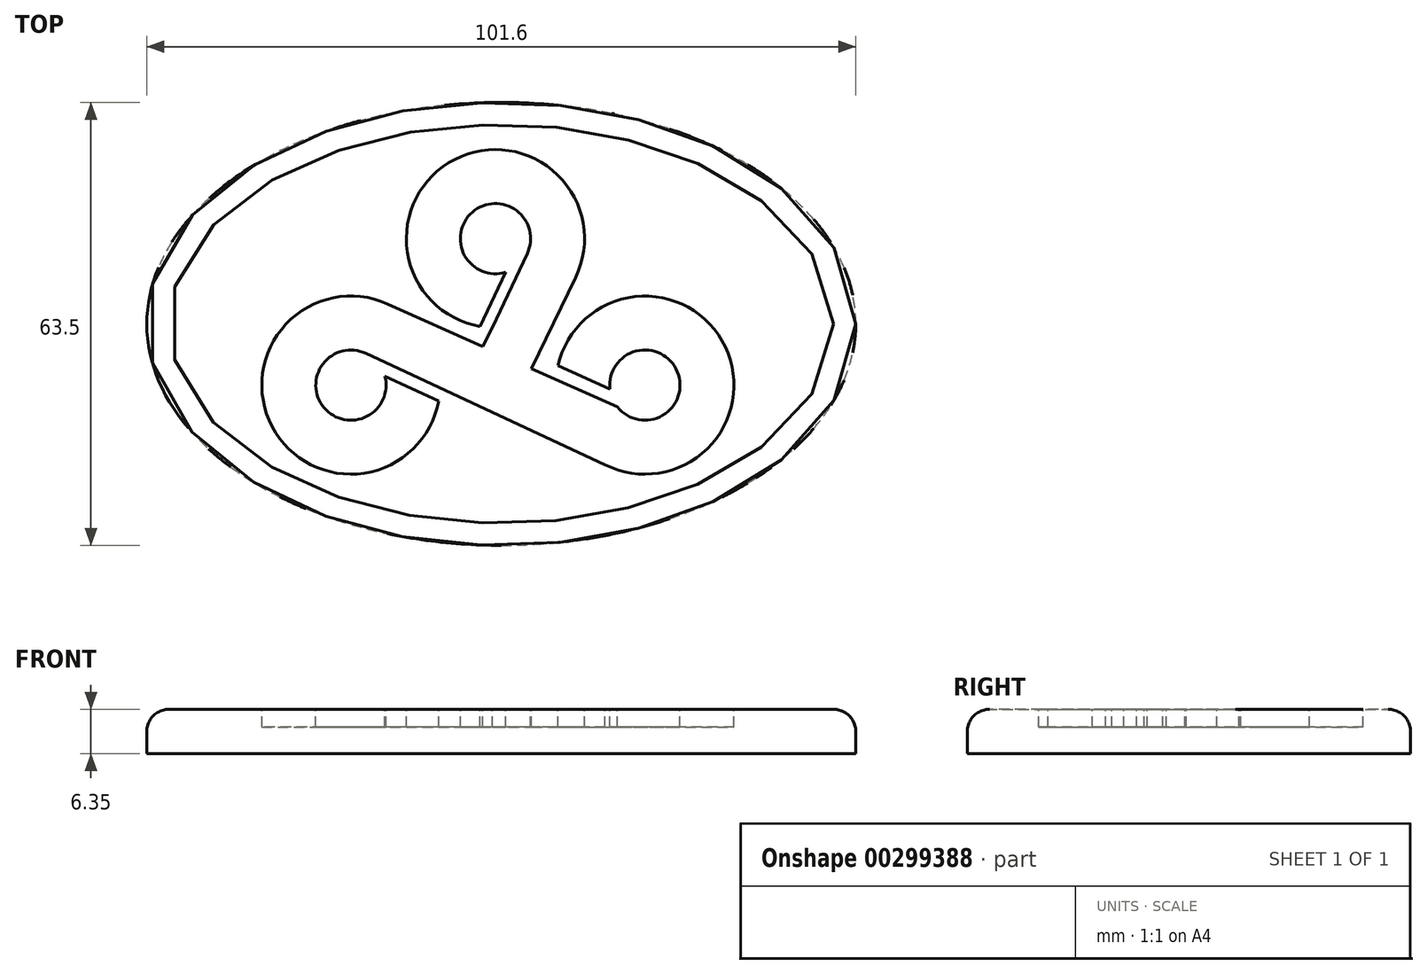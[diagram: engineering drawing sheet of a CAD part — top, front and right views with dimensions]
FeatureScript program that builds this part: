
annotation { "Feature Type Name" : "Feature", "Feature Type Description" : "" }
export const myFeature = defineFeature(function(context is Context, id is Id, definition is map)
    precondition{}
    {
        {
            var Q0;
            Q0=qCreatedBy(makeId("Top.planeOp"),FACE);
            var sketch = newSketch(context, id + "F0", { "sketchPlane" : qUnion([Q0])});
            skEllipse(sketch, "E0", {"center": v(-4.33, 14.7) * mm, "majorRadius": 50.8 * mm, "minorRadius": 31.75 * mm, "majorAxis": v(1, 0)});
            skSolve(sketch);
        }
        {
            var Q0;
            Q0=makeQuery(id+"F0.imprint","IMPRINT",FACE,{"disambiguationData":[TD([[makeQuery(id+"F0.imprint","IMPRINT",EDGE,{"derivedFrom":sQuery(id+"F0.wireOp",EDGE,"E0")}),1.0]])]});
            extrude(context, id + "F1", {"entities" : qUnion([Q0]), "depth" : 6.35 * mm});
        }
        {
            var Q0;
            Q0=makeQuery(id+"F1.opExtrude","CAP_EDGE",EDGE,{"disambiguationData":[OSD([sQuery(id+"F0.wireOp",EDGE,"E0")])],"isStart":false});
            fillet(context, id + "F2", {"entities" : qUnion([Q0]), "radius" : 3.17 * mm, "tangentPropagation" : true, "allowEdgeOverflow" : false});
        }
        {
            var Q0;
            Q0=makeQuery(id+"F1.opExtrude","CAP_FACE",FACE,{"disambiguationData":[OSD([sQuery(id+"F0.wireOp",EDGE,"E0")])],"isStart":false});
            var sketch = newSketch(context, id + "F3", { "sketchPlane" : qUnion([Q0])});
            skArc(sketch, "E1", {"start": v(-20.66, 17.57) * mm, "mid": v(-37.18, -0.02) * mm, "end": v(-13.32, 3.64) * mm});
            skArc(sketch, "E2", {"start": v(-23.75, 10.48) * mm, "mid": v(-29.73, 2.69) * mm, "end": v(-21.02, 7.22) * mm});
            skArc(sketch, "E3", {"start": v(6.32, 21.35) * mm, "mid": v(-11, 38.28) * mm, "end": v(-7.35, 14.34) * mm});
            skArc(sketch, "E4", {"start": v(-0.61, 24.78) * mm, "mid": v(-8.46, 30.72) * mm, "end": v(-3.7, 22.1) * mm});
            skArc(sketch, "E5", {"start": v(10.55, -5.5) * mm, "mid": v(27.78, 11.4) * mm, "end": v(3.8, 8.7) * mm});
            skArc(sketch, "E6", {"start": v(12.32, 2.79) * mm, "mid": v(20.9, 7.84) * mm, "end": v(11.25, 5.37) * mm});
            skLineSegment(sketch, "E7", {"start": v(-5.6, 14.16) * mm, "end": v(-7.01, 11.46) * mm});
            skLineSegment(sketch, "E8", {"start": v(-7.01, 11.46) * mm, "end": v(-20.66, 17.57) * mm});
            skLineSegment(sketch, "E9", {"start": v(-20.66, 17.57) * mm, "end": v(-7.01, 11.46) * mm});
            skLineSegment(sketch, "E10", {"start": v(-5.6, 14.16) * mm, "end": v(-0.61, 24.78) * mm});
            skLineSegment(sketch, "E11", {"start": v(-7.35, 14.34) * mm, "end": v(-3.7, 22.1) * mm});
            skLineSegment(sketch, "E12", {"start": v(0, 8.3) * mm, "end": v(6.32, 21.35) * mm});
            skLineSegment(sketch, "E13", {"start": v(3.8, 8.7) * mm, "end": v(11.25, 5.37) * mm});
            skLineSegment(sketch, "E14", {"start": v(10.55, -5.5) * mm, "end": v(-23.75, 10.48) * mm});
            skLineSegment(sketch, "E15", {"start": v(-13.32, 3.64) * mm, "end": v(-21.02, 7.22) * mm});
            skLineSegment(sketch, "E16.trimOffspring", {"start": v(0, 8.3) * mm, "end": v(12.32, 2.79) * mm});
            skSolve(sketch);
        }
        {
            var Q0;
            Q0=makeQuery(id+"F3.imprint","IMPRINT",FACE,{"disambiguationData":[TD([[makeQuery(id+"F3.imprint","IMPRINT",EDGE,{"derivedFrom":sQuery(id+"F3.wireOp",EDGE,"E1")}),1.0]])]});
            extrude(context, id + "F4", {"entities" : qUnion([Q0]), "operationType" : NewBodyOperationType.REMOVE, "depth" : -2.54 * mm});
        }
    });
